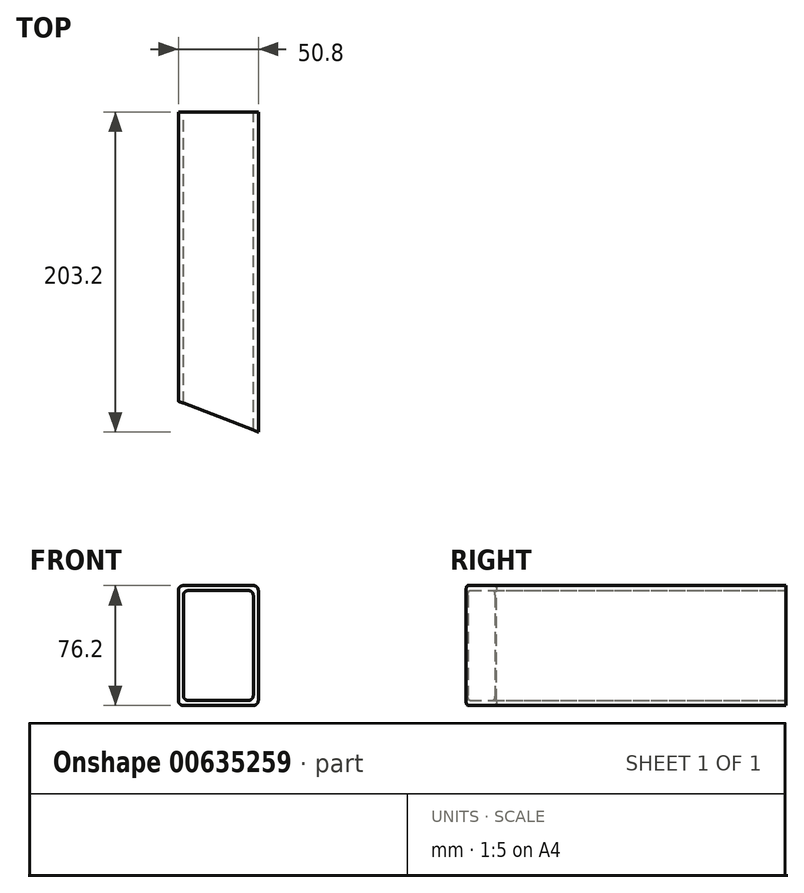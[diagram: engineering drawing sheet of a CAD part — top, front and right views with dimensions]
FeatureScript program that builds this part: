
annotation { "Feature Type Name" : "Feature", "Feature Type Description" : "" }
export const myFeature = defineFeature(function(context is Context, id is Id, definition is map)
    precondition{}
    {
        {
            var Q0;
            Q0=qCreatedBy(makeId("Front.planeOp"),FACE);
            var sketch = newSketch(context, id + "F0", { "sketchPlane" : qUnion([Q0])});
            skLineSegment(sketch, "E0.bottom", {"start": v(22.23, 38.1) * mm, "end": v(-22.23, 38.1) * mm});
            skLineSegment(sketch, "E0.top", {"start": v(22.23, -38.1) * mm, "end": v(-22.22, -38.1) * mm});
            skLineSegment(sketch, "E0.left", {"start": v(25.4, 34.93) * mm, "end": v(25.4, -34.93) * mm});
            skLineSegment(sketch, "E0.right", {"start": v(-25.4, 34.93) * mm, "end": v(-25.4, -34.93) * mm});
            skPoint(sketch, "E0.middle", {"position": v(0, 0) * mm});
            skLineSegment(sketch, "E1.0", {"start": v(19.05, 34.93) * mm, "end": v(-19.05, 34.93) * mm});
            skLineSegment(sketch, "E1.1", {"start": v(22.23, 31.75) * mm, "end": v(22.23, -31.75) * mm});
            skLineSegment(sketch, "E1.2", {"start": v(19.05, -34.93) * mm, "end": v(-19.05, -34.93) * mm});
            skLineSegment(sketch, "E1.3", {"start": v(-22.23, 31.75) * mm, "end": v(-22.22, -31.75) * mm});
            skPoint(sketch, "E2.visualSharp", {"position": v(-22.23, 34.93) * mm});
            skArc(sketch, "E2.filletArc", {"start": v(-19.05, 34.93) * mm, "mid": v(-21.3, 34) * mm, "end": v(-22.23, 31.75) * mm});
            skPoint(sketch, "E3.visualSharp", {"position": v(-25.4, 38.1) * mm});
            skArc(sketch, "E3.filletArc", {"start": v(-22.23, 38.1) * mm, "mid": v(-24.47, 37.17) * mm, "end": v(-25.4, 34.93) * mm});
            skPoint(sketch, "E4.visualSharp", {"position": v(22.23, 34.93) * mm});
            skArc(sketch, "E4.filletArc", {"start": v(22.22, 31.75) * mm, "mid": v(21.3, 34) * mm, "end": v(19.05, 34.92) * mm});
            skPoint(sketch, "E5.visualSharp", {"position": v(25.4, 38.1) * mm});
            skArc(sketch, "E5.filletArc", {"start": v(25.4, 34.93) * mm, "mid": v(24.47, 37.17) * mm, "end": v(22.23, 38.1) * mm});
            skPoint(sketch, "E6.visualSharp", {"position": v(-22.22, -34.93) * mm});
            skArc(sketch, "E6.filletArc", {"start": v(-22.22, -31.75) * mm, "mid": v(-21.3, -34) * mm, "end": v(-19.05, -34.93) * mm});
            skPoint(sketch, "E7.visualSharp", {"position": v(-25.4, -38.1) * mm});
            skArc(sketch, "E7.filletArc", {"start": v(-25.4, -34.93) * mm, "mid": v(-24.47, -37.17) * mm, "end": v(-22.22, -38.1) * mm});
            skPoint(sketch, "E8.visualSharp", {"position": v(22.23, -34.93) * mm});
            skArc(sketch, "E8.filletArc", {"start": v(19.05, -34.93) * mm, "mid": v(21.3, -34) * mm, "end": v(22.23, -31.75) * mm});
            skPoint(sketch, "E9.visualSharp", {"position": v(25.4, -38.1) * mm});
            skArc(sketch, "E9.filletArc", {"start": v(22.23, -38.1) * mm, "mid": v(24.47, -37.17) * mm, "end": v(25.4, -34.93) * mm});
            skSolve(sketch);
        }
        {
            var Q0;
            Q0 = qSketchRegion(id + "F0", true);
            extrude(context, id + "F1", {"entities" : qUnion([Q0]), "depth" : 203.2 * mm, "offsetDistance" : 25.4 * mm});
        }
        {
            var Q0;
            Q0=qCreatedBy(makeId("Top.planeOp"),FACE);
            var sketch = newSketch(context, id + "F2", { "sketchPlane" : qUnion([Q0])});
            skLineSegment(sketch, "E10.bottom", {"start": v(25.4, -203.2) * mm, "end": v(-25.4, -203.2) * mm});
            skLineSegment(sketch, "E10.right", {"start": v(-25.4, -203.2) * mm, "end": v(-25.4, -183.7) * mm});
            skPoint(sketch, "E10.middle", {"position": v(0, -193.45) * mm});
            skLineSegment(sketch, "E11", {"start": v(-25.4, -183.7) * mm, "end": v(25.4, -203.2) * mm});
            skPoint(sketch, "E10.left.end.orphan", {"position": v(25.4, -183.7) * mm});
            skSolve(sketch);
        }
        {
            var Q0;
            Q0 = qSketchRegion(id + "F2", true);
            extrude(context, id + "F3", {"entities" : qUnion([Q0]), "operationType" : NewBodyOperationType.REMOVE, "endBound" : BoundingType.THROUGH_ALL, "oppositeDirection" : true, "depth" : 25.4 * mm, "offsetDistance" : 25.4 * mm, "hasSecondDirection" : true, "secondDirectionBound" : SecondDirectionBoundingType.THROUGH_ALL, "secondDirectionOppositeDirection" : false, "secondDirectionDepth" : 25.4 * mm});
        }
    });
